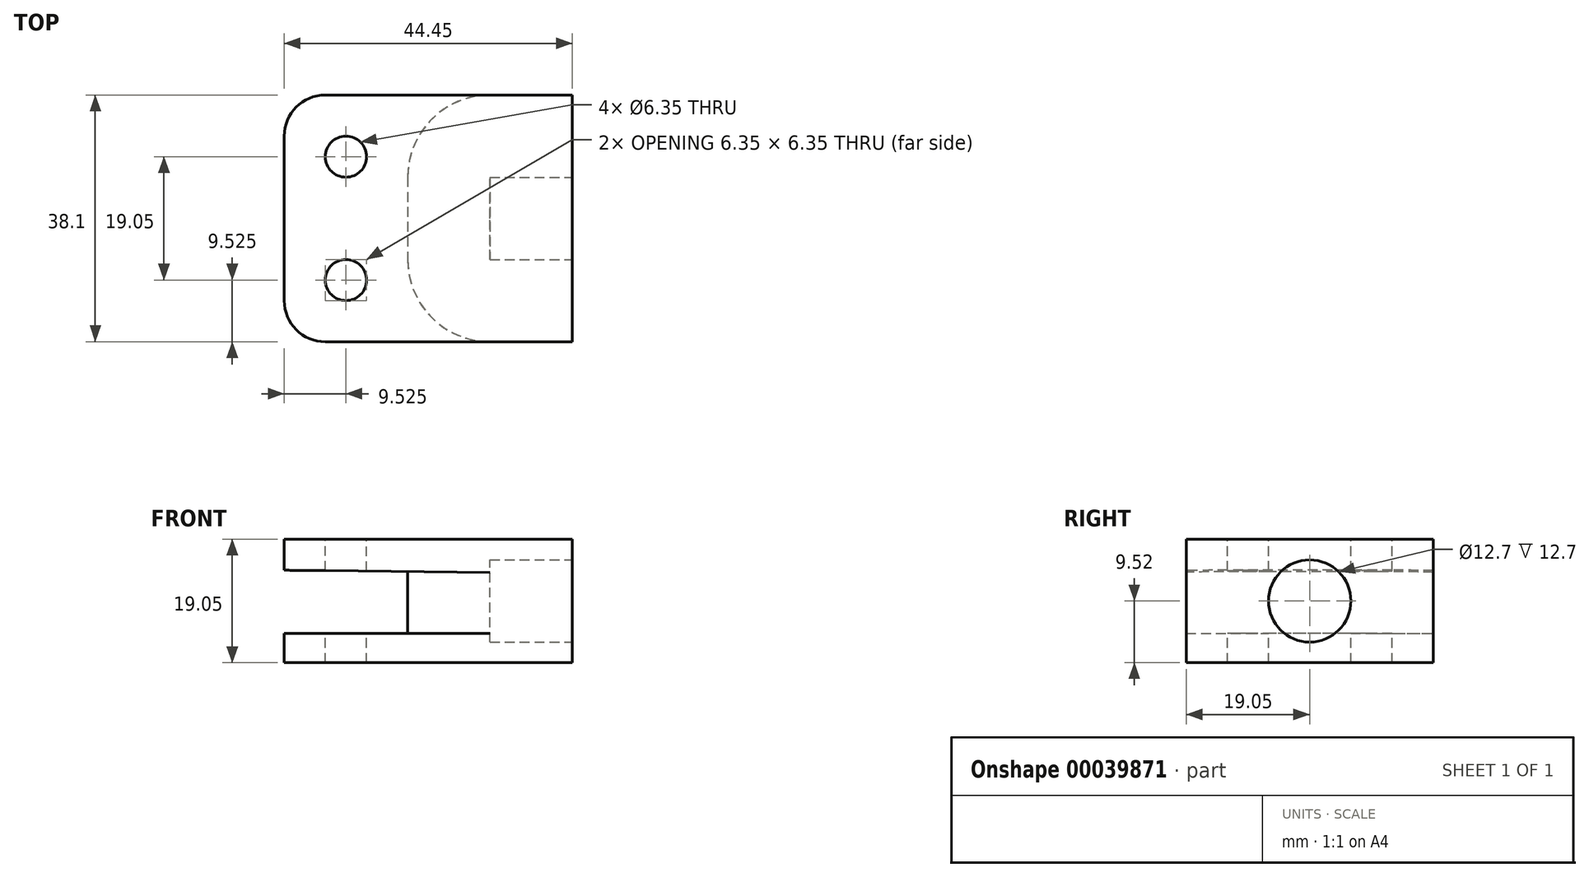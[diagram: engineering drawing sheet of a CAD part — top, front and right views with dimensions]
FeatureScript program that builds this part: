
annotation { "Feature Type Name" : "Feature", "Feature Type Description" : "" }
export const myFeature = defineFeature(function(context is Context, id is Id, definition is map)
    precondition{}
    {
        {
            var Q0;
            Q0=qCreatedBy(makeId("Front.planeOp"),FACE);
            var sketch = newSketch(context, id + "F0", { "sketchPlane" : qUnion([Q0])});
            skLineSegment(sketch, "E0", {"start": v(-44.45, 8.74) * mm, "end": v(-44.45, 13.52) * mm});
            skLineSegment(sketch, "E1", {"start": v(-44.45, 13.52) * mm, "end": v(0, 13.52) * mm});
            skLineSegment(sketch, "E2", {"start": v(0, 13.52) * mm, "end": v(0, -5.53) * mm});
            skLineSegment(sketch, "E3", {"start": v(0, -5.53) * mm, "end": v(-44.45, -5.53) * mm});
            skLineSegment(sketch, "E4", {"start": v(-44.45, -5.53) * mm, "end": v(-44.45, -1) * mm});
            skLineSegment(sketch, "E5", {"start": v(-44.45, -1) * mm, "end": v(-25.4, -1) * mm});
            skLineSegment(sketch, "E6", {"start": v(-25.4, -1) * mm, "end": v(-25.4, 8.53) * mm});
            skLineSegment(sketch, "E7", {"start": v(-25.4, 8.53) * mm, "end": v(-44.45, 8.74) * mm});
            skSolve(sketch);
        }
        {
            var Q0;
            Q0 = qSketchRegion(id + "F0", true);
            extrude(context, id + "F1", {"entities" : qUnion([Q0]), "oppositeDirection" : true, "depth" : 38.1 * mm});
        }
        {
            var Q0;
            Q0=makeQuery(id+"F1.opExtrude","SWEPT_FACE",FACE,{"disambiguationData":[OSD([sQuery(id+"F0.wireOp",EDGE,"E1")])]});
            var sketch = newSketch(context, id + "F2", { "sketchPlane" : qUnion([Q0])});
            skCircle(sketch, "E8", {"center": v(-34.93, 28.58) * mm, "radius": 3.18 * mm});
            skCircle(sketch, "E9", {"center": v(-34.93, 9.52) * mm, "radius": 3.18 * mm});
            skSolve(sketch);
        }
        {
            var Q0;
            Q0 = qSketchRegion(id + "F2", true);
            extrude(context, id + "F3", {"entities" : qUnion([Q0]), "operationType" : NewBodyOperationType.REMOVE, "oppositeDirection" : true, "depth" : 177.8 * mm});
        }
        {
            var Q0;
            Q0=makeQuery(id+"F1.opExtrude","CAP_EDGE",EDGE,{"disambiguationData":[OSD([sQuery(id+"F0.wireOp",EDGE,"E0")])],"isStart":false});
            var Q1;
            Q1=makeQuery(id+"F1.opExtrude","CAP_EDGE",EDGE,{"disambiguationData":[OSD([sQuery(id+"F0.wireOp",EDGE,"E4")])],"isStart":false});
            var Q2;
            Q2=makeQuery(id+"F1.opExtrude","CAP_EDGE",EDGE,{"disambiguationData":[OSD([sQuery(id+"F0.wireOp",EDGE,"E0")])],"isStart":true});
            var Q3;
            Q3=makeQuery(id+"F1.opExtrude","CAP_EDGE",EDGE,{"disambiguationData":[OSD([sQuery(id+"F0.wireOp",EDGE,"E4")])],"isStart":true});
            fillet(context, id + "F4", {"entities" : qUnion([Q0, Q1, Q2, Q3]), "radius" : 6.35 * mm, "tangentPropagation" : true, "allowEdgeOverflow" : false});
        }
        {
            var Q0;
            Q0=makeQuery(id+"F1.opExtrude","SWEPT_FACE",FACE,{"disambiguationData":[OSD([sQuery(id+"F0.wireOp",EDGE,"E2")])]});
            var sketch = newSketch(context, id + "F5", { "sketchPlane" : qUnion([Q0])});
            skLineSegment(sketch, "E10", {"start": v(0, 4) * mm, "end": v(38.1, 4) * mm});
            skCircle(sketch, "E11", {"center": v(19.05, 4) * mm, "radius": 6.35 * mm});
            skSolve(sketch);
        }
        {
            var Q0;
            Q0 = qSketchRegion(id + "F5", true);
            extrude(context, id + "F6", {"entities" : qUnion([Q0]), "operationType" : NewBodyOperationType.REMOVE, "oppositeDirection" : true, "depth" : 12.7 * mm});
        }
        {
            var Q0;
            Q0=makeQuery(id+"F1.opExtrude","CAP_EDGE",EDGE,{"disambiguationData":[OSD([sQuery(id+"F0.wireOp",EDGE,"E6")])],"isStart":true});
            var Q1;
            Q1=makeQuery(id+"F1.opExtrude","CAP_EDGE",EDGE,{"disambiguationData":[OSD([sQuery(id+"F0.wireOp",EDGE,"E6")])],"isStart":false});
            fillet(context, id + "F7", {"entities" : qUnion([Q0, Q1]), "radius" : 12.7 * mm, "tangentPropagation" : true, "allowEdgeOverflow" : false});
        }
    });
